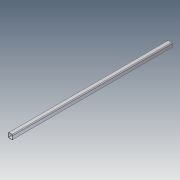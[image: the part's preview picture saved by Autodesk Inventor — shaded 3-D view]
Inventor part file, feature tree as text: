
AUTODESK INVENTOR PART (.ipt)
format: ipt  version: unknown  size: 178,688 bytes
history: native  units: in
note: dims shown in document units (in); Inventor stores cm internally (conversion verified against a paired STEP export)
features: extrude x1, sketch x1
ambient origin geometry x8: Origin, YZ Plane, XZ Plane, XY Plane, X Axis, Y Axis, Z Axis, Center Point
bodies: Solid1 (feature_tree)
feature tree (2):
  extrude  "Extrusion1"  Depth=0.25in
  sketch  "Sketch1"  dims[d0=1.5in d1=0.25in d2=0.125in d4=49.875in d5=0.0in]
